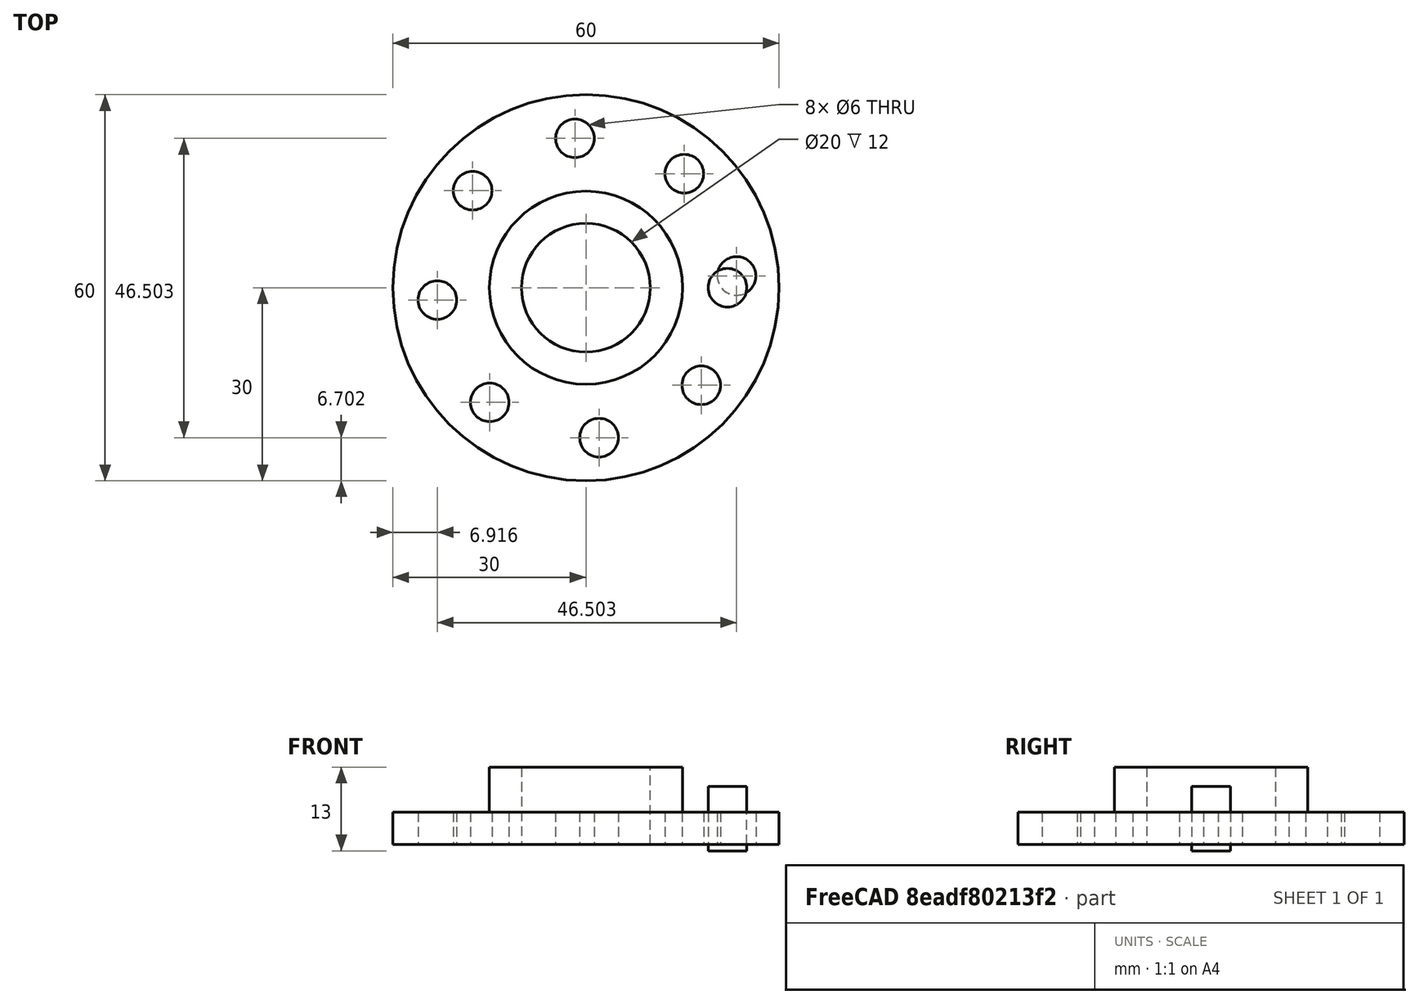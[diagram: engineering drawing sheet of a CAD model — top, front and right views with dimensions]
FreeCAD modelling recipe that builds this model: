
FCSTD DOCUMENT  (FreeCAD 1.0R39319 (Git))
Label: ojt1_t11p01_flangs
License: All rights reserved
LicenseURL: https://en.wikipedia.org/wiki/All_rights_reserved
objects: Part::Cylinder×4, Part::Cut×2, Part::Fuse×1, Part::FeaturePython×1
note: 7 computed .brp shape members not serialized (recipe doc carries the construction recipe); baked Part::Feature solids carry a one-line shape summary decoded from their .brp

FEATURE [Part::Cylinder] Cylinder
  Angle = 360
  AttacherType = Attacher::AttachEngine3D
  FirstAngle = 0
  Height = 5
  Radius = 30
  SecondAngle = 0
FEATURE [Part::Cylinder] Cylinder001
  Angle = 360
  AttacherType = Attacher::AttachEngine3D
  FirstAngle = 0
  Height = 12
  Radius = 15
  SecondAngle = 0
FEATURE [Part::Cylinder] Cylinder002
  Angle = 360
  AttacherType = Attacher::AttachEngine3D
  FirstAngle = 0
  Height = 30
  Placement = pos=(0,0,-1) rot=(0,0,1;0rad)
  Radius = 10
  SecondAngle = 0
FEATURE [Part::Fuse] Fusion
  Base = -> Cylinder
  Refine = true
  Tool = -> Cylinder001
FEATURE [Part::Cut] Cut
  Base = -> Fusion
  Refine = true
  Tool = -> Cylinder002
FEATURE [Part::Cylinder] Cylinder003
  Angle = 360
  AttacherType = Attacher::AttachEngine3D
  FirstAngle = 0
  Height = 10
  Placement = pos=(22,0,-1) rot=(0,0,1;0rad)
  Radius = 3
  SecondAngle = 0
FEATURE [Part::FeaturePython] Array  # Draft array (typed FeaturePython)
  AlwaysSyncPlacement = false
  Angle = 360
  ArrayType = 1
  Axis = (0,0,8)
  Base = -> Cylinder003
  Center = (45,3.89,0)
  Count = 8
  ExpandArray = false
  Fuse = false
  IntervalAxis = (0,0,0)
  IntervalX = (50,0,0)
  IntervalY = (0,50,0)
  IntervalZ = (0,0,50)
  NumberCircles = 3
  NumberPolar = 8
  NumberX = 2
  NumberY = 2
  NumberZ = 1
  Placement = pos=(-45,0,0) rot=(0,0,1;-0.087266rad)
  PlacementList = 8 placements: [(22,0,-1),(31.4872,-15.1241,-1),(48.89,-19.11,-1),(64.0141,-9.62281,-1),(68,7.78,-1),(58.5128,22.9041,-1),(41.11,26.89,-1),(25.9859,17.4028,-1)]
  RadialDistance = 50
  ScaleList = (8) [(1,1,1),(1,1,1),(1,1,1),(1,1,1),(1,1,1),(1,1,1),(1,1,1),(1,1,1)]
  Symmetry = 1
  TangentialDistance = 25
FEATURE [Part::Cut] Cut001
  Base = -> Cut
  Refine = true
  Tool = -> Array
